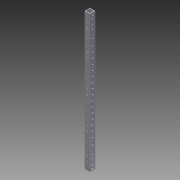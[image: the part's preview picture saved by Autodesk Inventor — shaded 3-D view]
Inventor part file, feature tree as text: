
AUTODESK INVENTOR PART (.ipt)
format: ipt  version: 2013 (Build 170138000, 138)  size: 201,216 bytes
history: native  units: in
note: dims shown in document units (in); Inventor stores cm internally (conversion verified against a paired STEP export)
features: extrude x4, sketch x4, reference x4
ambient origin geometry x8: Origin, YZ Plane, XZ Plane, XY Plane, X Axis, Y Axis, Z Axis, Center Point
bodies: Solid1 (feature_tree)
feature tree (12):
  extrude  "Extrusion1"  Depth=1.0in
  extrude  "Extrusion2"  Depth=26.0in TaperAngle=0.0deg
  extrude  "Extrusion3"  Depth=1.5in
  extrude  "Extrusion4"  Depth=9.4488in
  sketch  "Sketch1"  dims[d0=1.0in d1=1.0in]
  sketch  "Sketch2"  dims[d2=0.125in d3=26.0in d4=0.0in]
  sketch  "Sketch3"  dims[d5=0.225in d6=1.5in]
  reference  "Reference5"
  reference  "Reference6"
  reference  "Reference7"
  reference  "Reference8"
  sketch  "Sketch4"  dims[d7=26.0in d8=9.4488in d10=1.0in d11=0.3937in d13=1.0in d15=1.0in d16=0.0in d17=0.26in d25=1.0in d26=0.0in d27=0.26in d28=0.26in d29=4.25in d30=4.25in d31=17.5in d32=1.25in d33=0.26in d34=6.2992in d36=1.0in d37=0.3937in d39=1.0in d41=1.0in d42=0.75in d43=0.26in d45=1.0in d46=0.75in d47=1.0in d48=0.0in]
